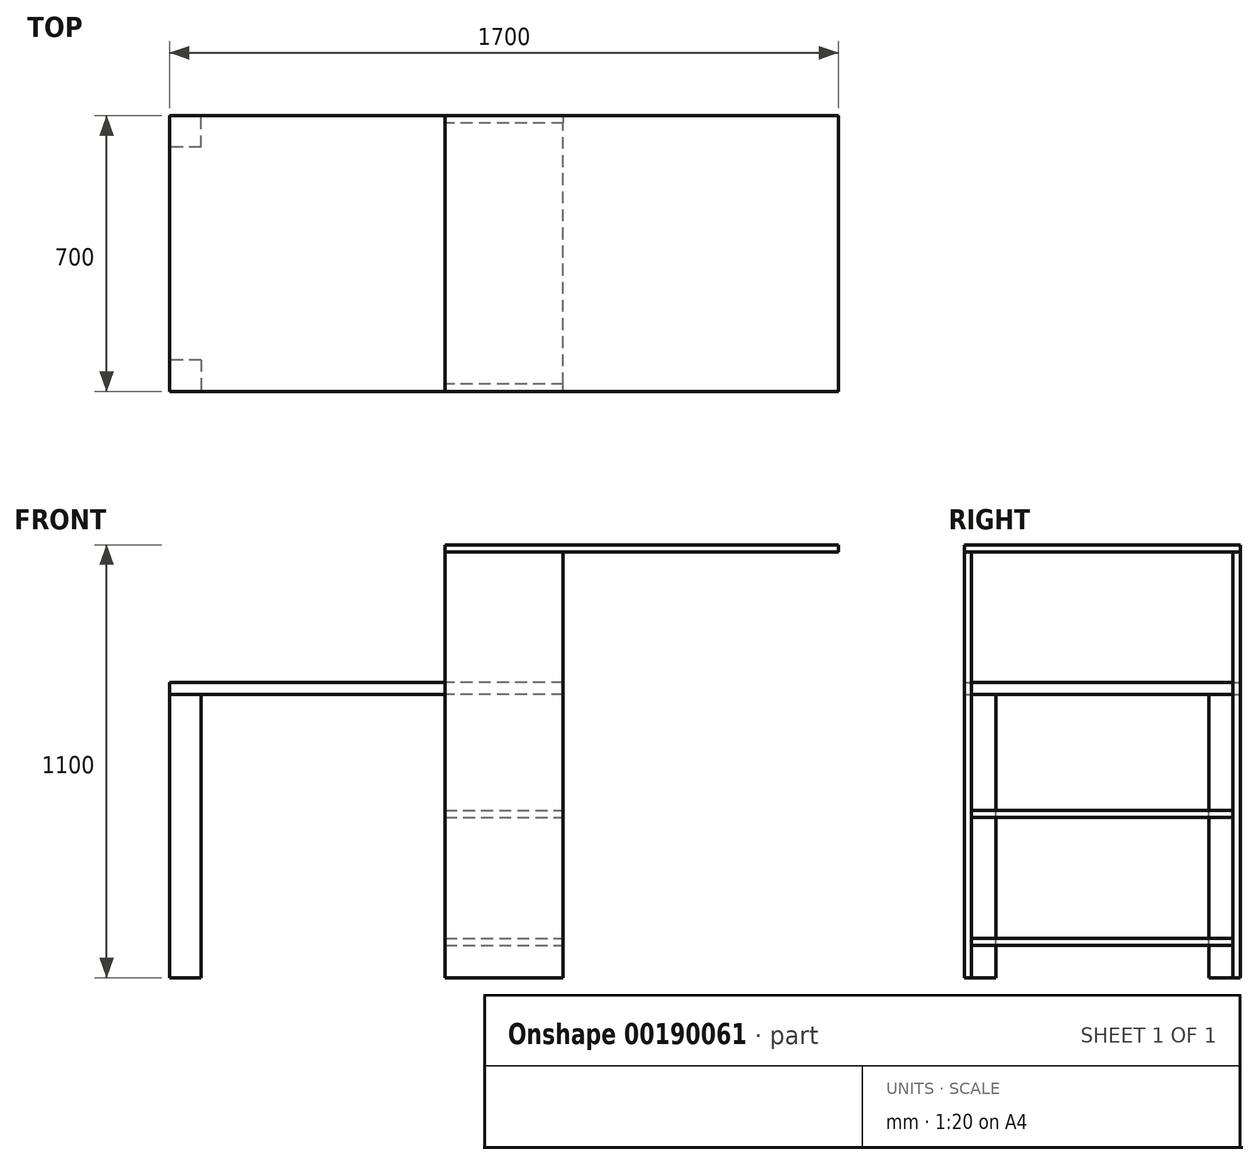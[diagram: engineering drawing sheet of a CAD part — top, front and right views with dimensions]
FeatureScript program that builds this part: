
annotation { "Feature Type Name" : "Feature", "Feature Type Description" : "" }
export const myFeature = defineFeature(function(context is Context, id is Id, definition is map)
    precondition{}
    {
        {
            var Q0;
            Q0=qCreatedBy(makeId("Top.planeOp"),FACE);
            var sketch = newSketch(context, id + "F0", { "sketchPlane" : qUnion([Q0])});
            skLineSegment(sketch, "E0.bottom", {"start": v(0, 350) * mm, "end": v(-300, 350) * mm});
            skLineSegment(sketch, "E0.top", {"start": v(0, 332) * mm, "end": v(-300, 332) * mm});
            skLineSegment(sketch, "E0.left", {"start": v(0, 350) * mm, "end": v(0, 332) * mm});
            skLineSegment(sketch, "E0.right", {"start": v(-300, 350) * mm, "end": v(-300, 332) * mm});
            skSolve(sketch);
        }
        {
            var Q0;
            Q0 = qSketchRegion(id + "F0", true);
            extrude(context, id + "F1", {"entities" : qUnion([Q0]), "depth" : 1082 * mm});
        }
        {
            var Q0;
            Q0=makeQuery(id+"F1.opExtrude","SWEPT_BODY",BODY,{"disambiguationData":[OSD([sQuery(id+"F0.wireOp",EDGE,"E0.bottom"),sQuery(id+"F0.wireOp",EDGE,"E0.top"),sQuery(id+"F0.wireOp",EDGE,"E0.left"),sQuery(id+"F0.wireOp",EDGE,"E0.right")])]});
            var Q1;
            Q1=qCreatedBy(makeId("Front.planeOp"),FACE);
            mirror(context, id + "F2", {"entities" : qUnion([Q0]), "mirrorPlane" : qUnion([Q1])});
        }
        {
            var Q0;
            Q0=makeQuery(id+"F2.opPattern","COPY",FACE,{"derivedFrom":makeQuery(id+"F1.opExtrude","SWEPT_FACE",FACE,{"disambiguationData":[OSD([sQuery(id+"F0.wireOp",EDGE,"E0.right")])]}),"instanceName":"1"});
            var sketch = newSketch(context, id + "F3", { "sketchPlane" : qUnion([Q0])});
            skLineSegment(sketch, "E1.bottom", {"start": v(-350, 1082) * mm, "end": v(350, 1082) * mm});
            skLineSegment(sketch, "E1.top", {"start": v(-350, 1100) * mm, "end": v(350, 1100) * mm});
            skLineSegment(sketch, "E1.left", {"start": v(-350, 1082) * mm, "end": v(-350, 1100) * mm});
            skLineSegment(sketch, "E1.right", {"start": v(350, 1082) * mm, "end": v(350, 1100) * mm});
            skSolve(sketch);
        }
        {
            var Q0;
            Q0 = qSketchRegion(id + "F3", true);
            extrude(context, id + "F4", {"entities" : qUnion([Q0]), "oppositeDirection" : true, "depth" : 1000 * mm});
        }
        {
            var Q0;
            Q0=qCreatedBy(makeId("Top.planeOp"),FACE);
            cPlane(context, id + "F5", {"entities" : qUnion([Q0]), "cplaneType" : CPlaneType.OFFSET, "offset" : 750 * mm, "width" : 150 * mm, "height" : 150 * mm});
        }
        {
            var Q0;
            Q0=qCreatedBy(id+"F5.planeOp",FACE);
            var sketch = newSketch(context, id + "F6", { "sketchPlane" : qUnion([Q0])});
            skLineSegment(sketch, "E2", {"start": v(0, 332) * mm, "end": v(-300, 332) * mm});
            skLineSegment(sketch, "E3", {"start": v(-300, 332) * mm, "end": v(-300, 350) * mm});
            skLineSegment(sketch, "E4", {"start": v(-300, 350) * mm, "end": v(-1000, 350) * mm});
            skLineSegment(sketch, "E5", {"start": v(-1000, 350) * mm, "end": v(-1000, -350) * mm});
            skLineSegment(sketch, "E6", {"start": v(-1000, -350) * mm, "end": v(-300, -350) * mm});
            skLineSegment(sketch, "E7", {"start": v(-300, -350) * mm, "end": v(-300, -332) * mm});
            skLineSegment(sketch, "E8", {"start": v(-300, -332) * mm, "end": v(0, -332) * mm});
            skLineSegment(sketch, "E9", {"start": v(0, -332) * mm, "end": v(0, 332) * mm});
            skSolve(sketch);
        }
        {
            var Q0;
            Q0 = qSketchRegion(id + "F6", true);
            extrude(context, id + "F7", {"entities" : qUnion([Q0]), "oppositeDirection" : true, "depth" : 30 * mm});
        }
        {
            var Q0;
            Q0=makeQuery(id+"F1.opExtrude","SWEPT_FACE",FACE,{"disambiguationData":[OSD([sQuery(id+"F0.wireOp",EDGE,"E0.left")])]});
            var sketch = newSketch(context, id + "F8", { "sketchPlane" : qUnion([Q0])});
            skLineSegment(sketch, "E10.bottom", {"start": v(-332, 82) * mm, "end": v(332, 82) * mm});
            skLineSegment(sketch, "E10.top", {"start": v(-332, 100) * mm, "end": v(332, 100) * mm});
            skLineSegment(sketch, "E10.left", {"start": v(-332, 82) * mm, "end": v(-332, 100) * mm});
            skLineSegment(sketch, "E10.right", {"start": v(332, 82) * mm, "end": v(332, 100) * mm});
            skLineSegment(sketch, "E11.bottom", {"start": v(-332, 425) * mm, "end": v(332, 425) * mm});
            skLineSegment(sketch, "E11.top", {"start": v(-332, 407) * mm, "end": v(332, 407) * mm});
            skLineSegment(sketch, "E11.left", {"start": v(-332, 425) * mm, "end": v(-332, 407) * mm});
            skLineSegment(sketch, "E11.right", {"start": v(332, 425) * mm, "end": v(332, 407) * mm});
            skSolve(sketch);
        }
        {
            var Q0;
            Q0 = qSketchRegion(id + "F8", true);
            var Q1;
            Q1=makeQuery(id+"F2.opPattern","COPY",FACE,{"derivedFrom":makeQuery(id+"F1.opExtrude","SWEPT_FACE",FACE,{"disambiguationData":[OSD([sQuery(id+"F0.wireOp",EDGE,"E0.right")])]}),"instanceName":"1"});
            extrude(context, id + "F9", {"entities" : qUnion([Q0]), "endBound" : BoundingType.UP_TO_SURFACE, "oppositeDirection" : true, "endBoundEntityFace" : qUnion([Q1]), "depth" : 25 * mm});
        }
        {
            var Q0;
            Q0=makeQuery(id+"F7.opExtrude","CAP_FACE",FACE,{"disambiguationData":[OSD([sQuery(id+"F6.wireOp",EDGE,"E2"),sQuery(id+"F6.wireOp",EDGE,"E3"),sQuery(id+"F6.wireOp",EDGE,"E4"),sQuery(id+"F6.wireOp",EDGE,"E5"),sQuery(id+"F6.wireOp",EDGE,"E6"),sQuery(id+"F6.wireOp",EDGE,"E7"),sQuery(id+"F6.wireOp",EDGE,"E8"),sQuery(id+"F6.wireOp",EDGE,"E9")])],"isStart":false});
            var sketch = newSketch(context, id + "F10", { "sketchPlane" : qUnion([Q0])});
            skLineSegment(sketch, "E12.bottom", {"start": v(-1000, -350) * mm, "end": v(-920, -350) * mm});
            skLineSegment(sketch, "E12.top", {"start": v(-1000, -270) * mm, "end": v(-920, -270) * mm});
            skLineSegment(sketch, "E12.left", {"start": v(-1000, -350) * mm, "end": v(-1000, -270) * mm});
            skLineSegment(sketch, "E12.right", {"start": v(-920, -350) * mm, "end": v(-920, -270) * mm});
            skSolve(sketch);
        }
        {
            var Q0;
            Q0 = qSketchRegion(id + "F10", true);
            var Q1;
            Q1=qCreatedBy(makeId("Top.planeOp"),FACE);
            extrude(context, id + "F11", {"entities" : qUnion([Q0]), "endBound" : BoundingType.UP_TO_SURFACE, "endBoundEntityFace" : qUnion([Q1]), "depth" : 25 * mm});
        }
        {
            var Q0;
            Q0=makeQuery(id+"F11.opExtrude","SWEPT_BODY",BODY,{"disambiguationData":[OSD([sQuery(id+"F10.wireOp",EDGE,"E12.bottom"),sQuery(id+"F10.wireOp",EDGE,"E12.top"),sQuery(id+"F10.wireOp",EDGE,"E12.left"),sQuery(id+"F10.wireOp",EDGE,"E12.right")])]});
            var Q1;
            Q1=qCreatedBy(makeId("Front.planeOp"),FACE);
            mirror(context, id + "F12", {"entities" : qUnion([Q0]), "mirrorPlane" : qUnion([Q1])});
        }
    });
